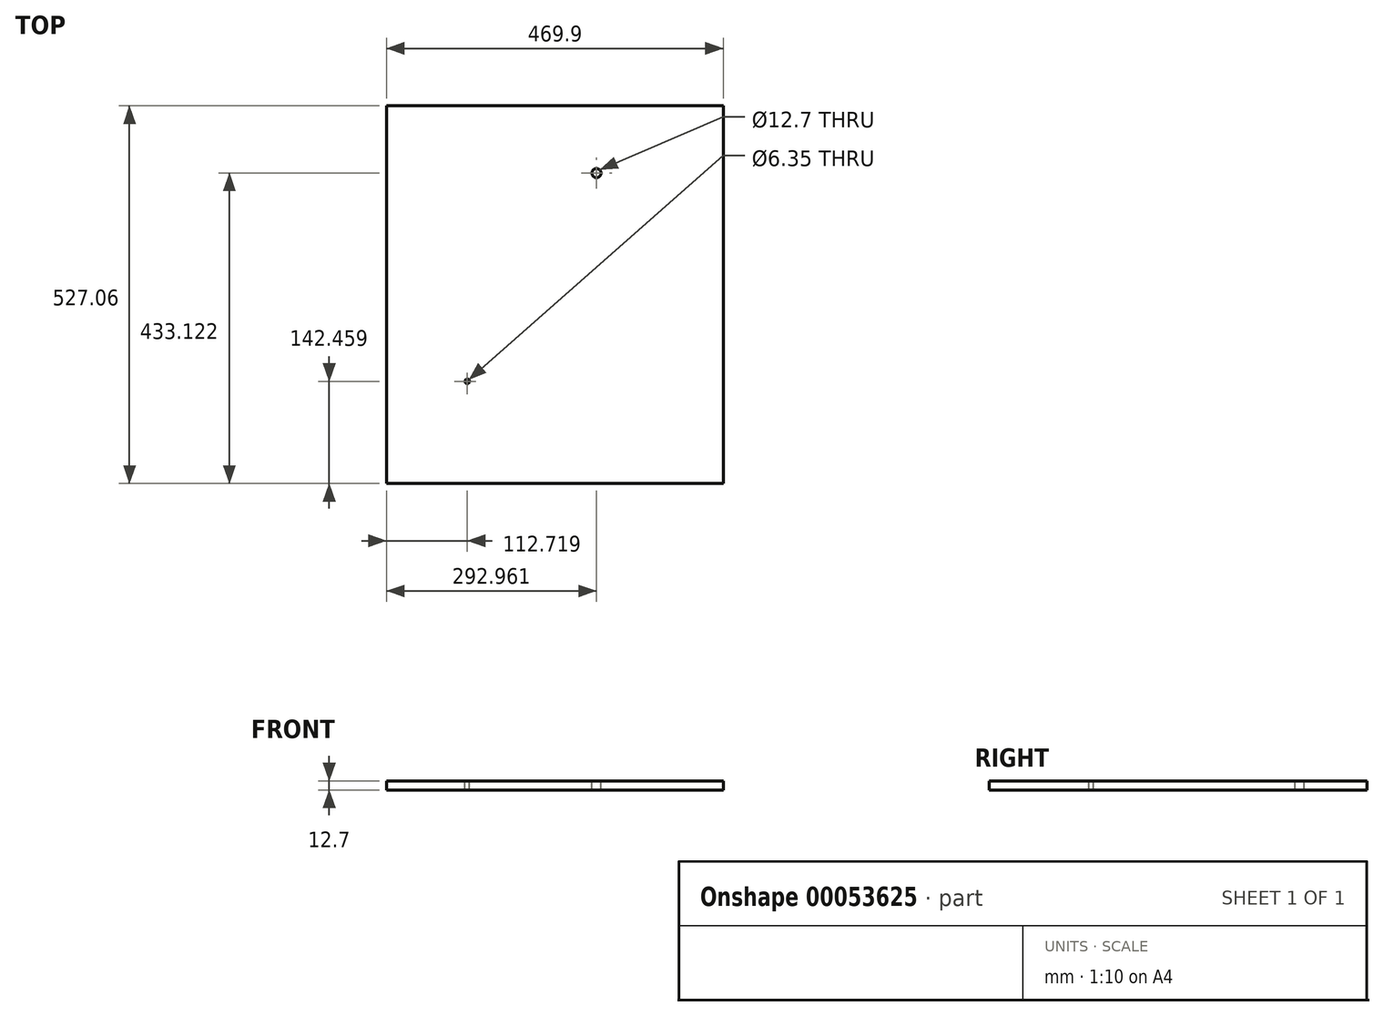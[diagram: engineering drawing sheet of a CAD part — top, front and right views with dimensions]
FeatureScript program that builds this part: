
annotation { "Feature Type Name" : "Feature", "Feature Type Description" : "" }
export const myFeature = defineFeature(function(context is Context, id is Id, definition is map)
    precondition{}
    {
        {
            var Q0;
            Q0=qCreatedBy(makeId("Top.planeOp"),FACE);
            var sketch = newSketch(context, id + "F0", { "sketchPlane" : qUnion([Q0])});
            skLineSegment(sketch, "E0.bottom", {"start": v(-234.95, -263.52) * mm, "end": v(234.95, -263.52) * mm});
            skLineSegment(sketch, "E0.top", {"start": v(-234.95, 263.53) * mm, "end": v(234.95, 263.53) * mm});
            skLineSegment(sketch, "E0.left", {"start": v(-234.95, -263.52) * mm, "end": v(-234.95, 263.53) * mm});
            skLineSegment(sketch, "E0.right", {"start": v(234.95, -263.52) * mm, "end": v(234.95, 263.53) * mm});
            skSolve(sketch);
        }
        {
            var Q0;
            Q0=makeQuery(id+"F0.imprint","IMPRINT",FACE,{"disambiguationData":[TD([[makeQuery(id+"F0.imprint","IMPRINT",EDGE,{"derivedFrom":sQuery(id+"F0.wireOp",EDGE,"E0.bottom")}),1.0]])]});
            extrude(context, id + "F1", {"entities" : qUnion([Q0]), "depth" : 12.7 * mm});
        }
        {
            var Q0;
            Q0=makeQuery(id+"F1.opExtrude","CAP_FACE",FACE,{"disambiguationData":[OSD([sQuery(id+"F0.wireOp",EDGE,"E0.bottom"),sQuery(id+"F0.wireOp",EDGE,"E0.top"),sQuery(id+"F0.wireOp",EDGE,"E0.left"),sQuery(id+"F0.wireOp",EDGE,"E0.right")])],"isStart":false});
            var sketch = newSketch(context, id + "F2", { "sketchPlane" : qUnion([Q0])});
            skCircle(sketch, "E1", {"center": v(-122.23, -121.07) * mm, "radius": 3.18 * mm});
            skCircle(sketch, "E2", {"center": v(58.01, 169.6) * mm, "radius": 6.35 * mm});
            skSolve(sketch);
        }
        {
            var Q0;
            Q0 = qSketchRegion(id + "F2", true);
            extrude(context, id + "F3", {"entities" : qUnion([Q0]), "operationType" : NewBodyOperationType.REMOVE, "endBound" : BoundingType.THROUGH_ALL, "oppositeDirection" : true, "depth" : 25.4 * mm});
        }
    });
